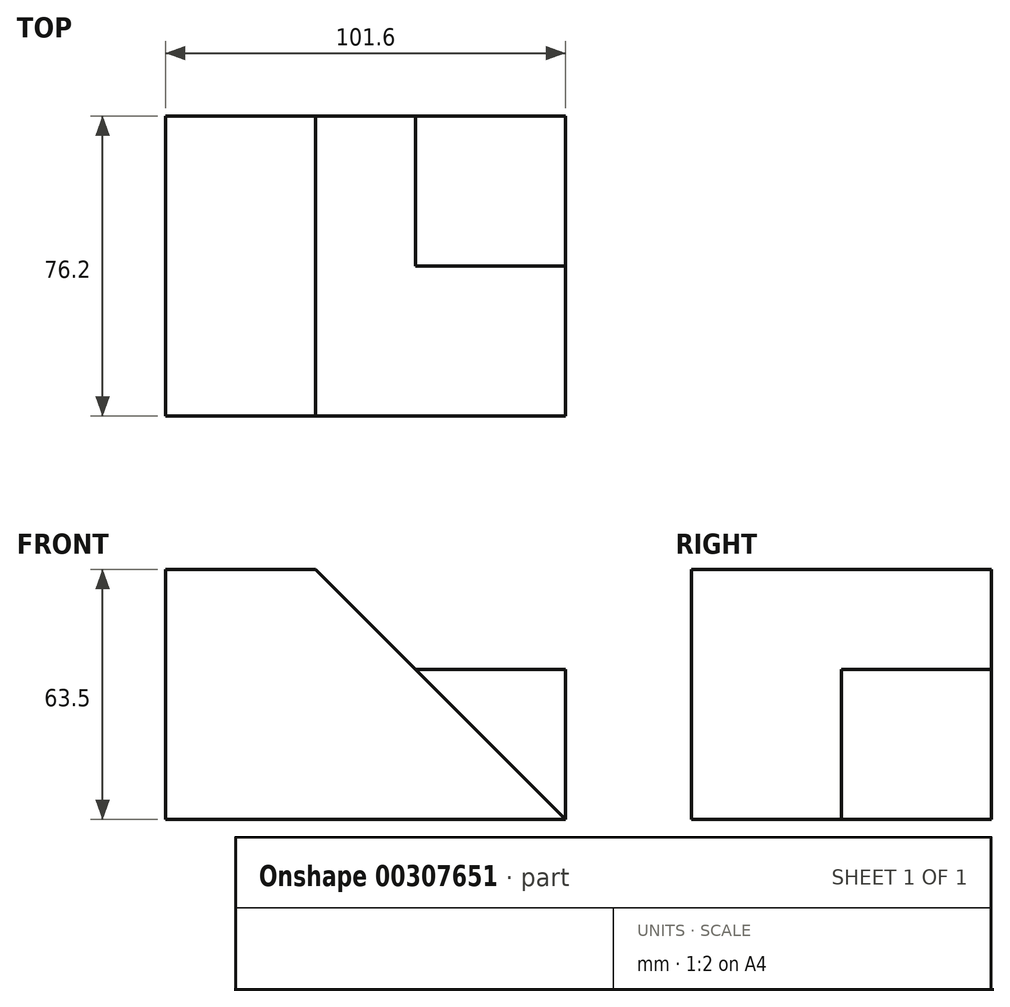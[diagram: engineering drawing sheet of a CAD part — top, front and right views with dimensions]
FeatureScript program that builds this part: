
annotation { "Feature Type Name" : "Feature", "Feature Type Description" : "" }
export const myFeature = defineFeature(function(context is Context, id is Id, definition is map)
    precondition{}
    {
        {
            var Q0;
            Q0=qCreatedBy(makeId("Front.planeOp"),FACE);
            var sketch = newSketch(context, id + "F0", { "sketchPlane" : qUnion([Q0])});
            skLineSegment(sketch, "E0", {"start": v(-50.02, -46.72) * mm, "end": v(-50.02, 16.78) * mm});
            skLineSegment(sketch, "E1", {"start": v(-50.02, 16.78) * mm, "end": v(-11.92, 16.78) * mm});
            skLineSegment(sketch, "E2", {"start": v(-11.92, 16.78) * mm, "end": v(51.58, -46.72) * mm});
            skLineSegment(sketch, "E3", {"start": v(51.58, -46.72) * mm, "end": v(-50.02, -46.72) * mm});
            skSolve(sketch);
        }
        {
            var Q0;
            Q0=makeQuery(id+"F0.imprint","IMPRINT",FACE,{"disambiguationData":[TD([[makeQuery(id+"F0.imprint","IMPRINT",EDGE,{"derivedFrom":sQuery(id+"F0.wireOp",EDGE,"E0")}),-1.0]])]});
            extrude(context, id + "F1", {"entities" : qUnion([Q0]), "depth" : 76.2 * mm});
        }
        {
            var Q0;
            Q0=makeQuery(id+"F1.opExtrude","CAP_FACE",FACE,{"disambiguationData":[OSD([sQuery(id+"F0.wireOp",EDGE,"E0"),sQuery(id+"F0.wireOp",EDGE,"E1"),sQuery(id+"F0.wireOp",EDGE,"E2"),sQuery(id+"F0.wireOp",EDGE,"E3")])],"isStart":true});
            var sketch = newSketch(context, id + "F2", { "sketchPlane" : qUnion([Q0])});
            skLineSegment(sketch, "E4", {"start": v(-13.48, -8.62) * mm, "end": v(-51.58, -8.62) * mm});
            skLineSegment(sketch, "E5", {"start": v(-51.58, -8.62) * mm, "end": v(-51.58, -46.72) * mm});
            skLineSegment(sketch, "E6", {"start": v(-51.58, -46.72) * mm, "end": v(-13.48, -8.62) * mm});
            skSolve(sketch);
        }
        {
            var Q0;
            Q0=makeQuery(id+"F2.imprint","IMPRINT",FACE,{"disambiguationData":[TD([[makeQuery(id+"F2.imprint","IMPRINT",EDGE,{"derivedFrom":sQuery(id+"F2.wireOp",EDGE,"E4")}),1.0]])]});
            extrude(context, id + "F3", {"entities" : qUnion([Q0]), "depth" : -38.1 * mm});
        }
    });
